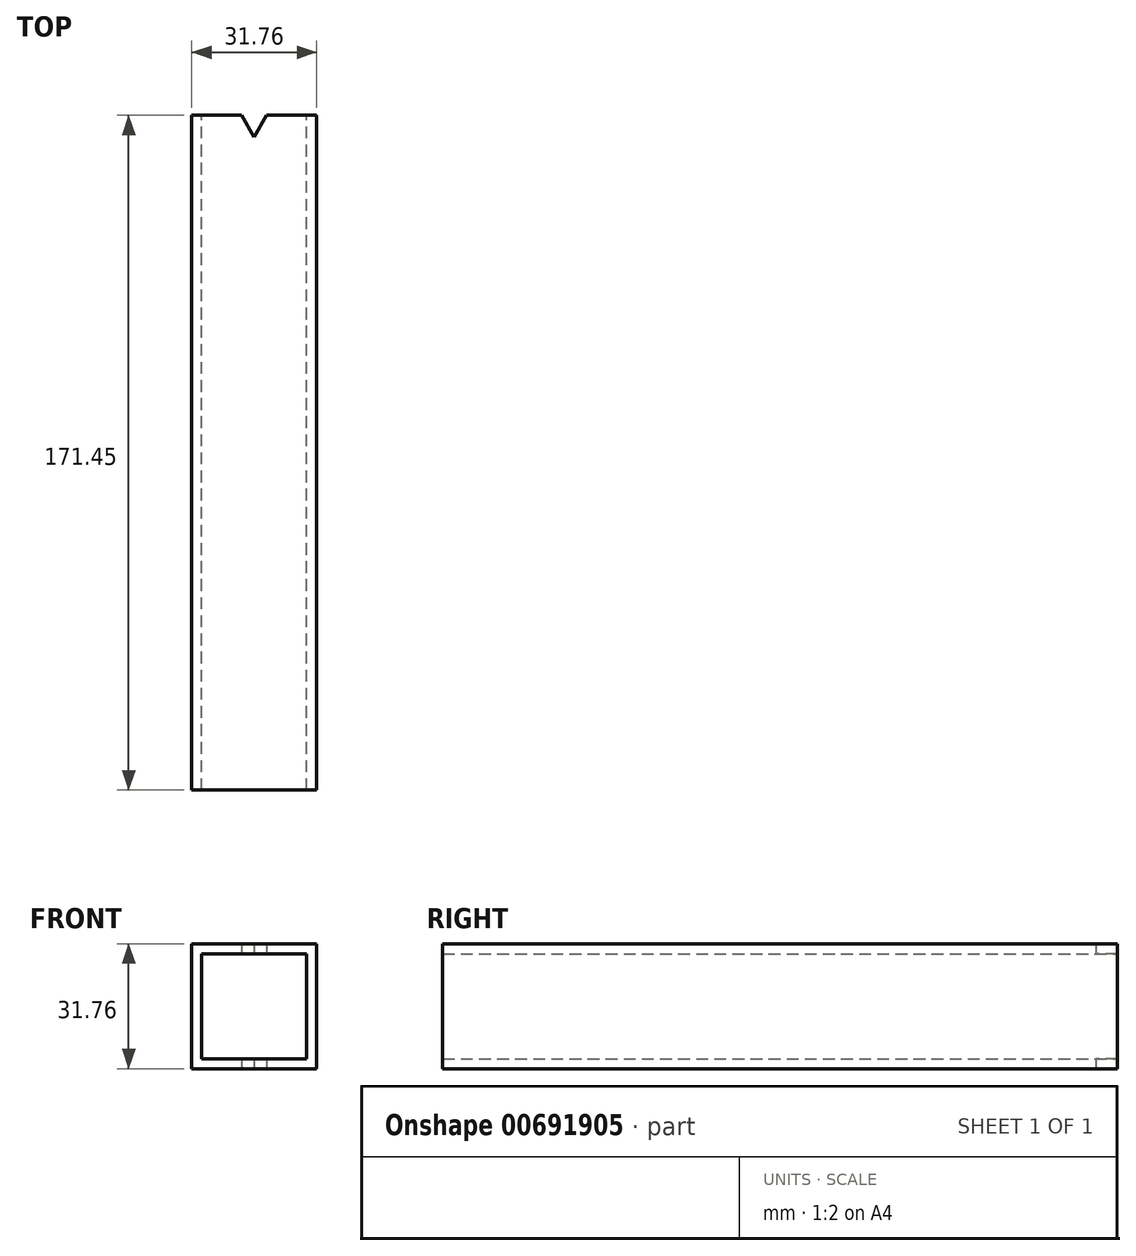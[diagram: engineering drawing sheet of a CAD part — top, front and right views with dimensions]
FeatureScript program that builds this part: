
annotation { "Feature Type Name" : "Feature", "Feature Type Description" : "" }
export const myFeature = defineFeature(function(context is Context, id is Id, definition is map)
    precondition{}
    {
        {
            var Q0;
            Q0=qCreatedBy(makeId("Front.planeOp"),FACE);
            var sketch = newSketch(context, id + "F0", { "sketchPlane" : qUnion([Q0])});
            skLineSegment(sketch, "E0.bottom", {"start": v(15.88, -15.88) * mm, "end": v(-15.88, -15.88) * mm});
            skLineSegment(sketch, "E0.top", {"start": v(15.88, 15.88) * mm, "end": v(-15.87, 15.87) * mm});
            skLineSegment(sketch, "E0.left", {"start": v(15.88, -15.88) * mm, "end": v(15.88, 15.88) * mm});
            skLineSegment(sketch, "E0.right", {"start": v(-15.88, -15.88) * mm, "end": v(-15.88, 15.88) * mm});
            skPoint(sketch, "E0.middle", {"position": v(0, 0) * mm});
            skLineSegment(sketch, "E1.bottom", {"start": v(13.33, -13.34) * mm, "end": v(-13.33, -13.34) * mm});
            skLineSegment(sketch, "E1.top", {"start": v(13.33, 13.34) * mm, "end": v(-13.33, 13.34) * mm});
            skLineSegment(sketch, "E1.left", {"start": v(13.33, -13.34) * mm, "end": v(13.33, 13.33) * mm});
            skLineSegment(sketch, "E1.right", {"start": v(-13.33, -13.34) * mm, "end": v(-13.33, 13.34) * mm});
            skSolve(sketch);
        }
        {
            var Q0;
            Q0=makeQuery(id+"F0.imprint","IMPRINT",FACE,{"disambiguationData":[TD([[makeQuery(id+"F0.imprint","IMPRINT",EDGE,{"derivedFrom":sQuery(id+"F0.wireOp",EDGE,"E0.bottom")}),-1.0]])]});
            extrude(context, id + "F1", {"entities" : qUnion([Q0]), "endBound" : BoundingType.SYMMETRIC, "depth" : 171.45 * mm, "offsetDistance" : 25.4 * mm});
        }
        {
            var Q0;
            Q0=makeQuery(id+"F1.opExtrude","SWEPT_FACE",FACE,{"disambiguationData":[OSD([sQuery(id+"F0.wireOp",EDGE,"E0.bottom")])]});
            var sketch = newSketch(context, id + "F2", { "sketchPlane" : qUnion([Q0])});
            skLineSegment(sketch, "E2", {"start": v(-3.18, -85.73) * mm, "end": v(3.17, -85.73) * mm});
            skLineSegment(sketch, "E3", {"start": v(3.18, -85.73) * mm, "end": v(0, -80.23) * mm});
            skLineSegment(sketch, "E4", {"start": v(0, -80.23) * mm, "end": v(-3.18, -85.73) * mm});
            skSolve(sketch);
        }
        {
            var Q0;
            Q0=makeQuery(id+"F2.imprint","IMPRINT",FACE,{"disambiguationData":[TD([[makeQuery(id+"F2.imprint","IMPRINT",EDGE,{"derivedFrom":sQuery(id+"F2.wireOp",EDGE,"E2")}),-1.0]])]});
            var Q1;
            Q1=makeQuery(id+"F1.opExtrude","SWEPT_FACE",FACE,{"disambiguationData":[OSD([sQuery(id+"F0.wireOp",EDGE,"E0.top")])]});
            extrude(context, id + "F3", {"entities" : qUnion([Q0]), "operationType" : NewBodyOperationType.REMOVE, "endBound" : BoundingType.UP_TO_SURFACE, "oppositeDirection" : true, "depth" : 25.4 * mm, "endBoundEntityFace" : qUnion([Q1]), "offsetDistance" : 25.4 * mm});
        }
    });
